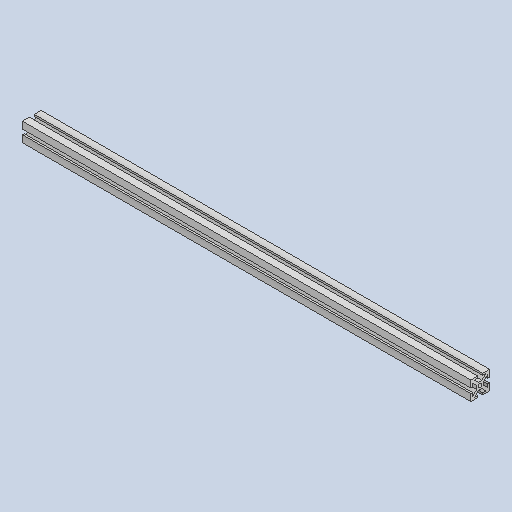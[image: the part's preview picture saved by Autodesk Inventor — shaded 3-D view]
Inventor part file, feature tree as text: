
AUTODESK INVENTOR PART (.ipt)
format: ipt  version: 2023 (Build 270158030, 158C)  size: 144,896 bytes
history: native  units: in
note: dims shown in document units (in); Inventor stores cm internally (conversion verified against a paired STEP export)
features: extrude x1, sketch x1
ambient origin geometry x8: Origin, YZ Plane, XZ Plane, XY Plane, X Axis, Y Axis, Z Axis, Center Point
bodies: Solid1 (feature_tree)
feature tree (2):
  extrude  "Extrusion1"  Depth=0.0975in
  sketch  "Sketch1"  dims[d2=0.37in d3=0.0975in d7=0.0975in d10=0.0975in d11=1.0in d13=0.0975in d16=0.0975in d17=0.37in d18=1.0in d23=0.0975in d24=1.0in d25=1.0in d32=0.175in d33=0.175in d35=135.0deg d36=0.175in d37=0.175in d38=0.0975in d40=0.175in d41=0.175in d42=0.175in d43=0.175in d44=0.2in d45=24.0in d46=0.0in]
